# Revit family: 63_UN_Trunk_Maxos Fusion Trunk_Signify
name_source: partatom
category: Lighting Fixtures
units: mm (PartAtom-declared; Revit-internal decimal feet)

## family parameters
Always vertical = Yes
Cut with Voids When Loaded = No
Light Source = No
OmniClass Number = 23.80.70.11.14.11
OmniClass Title = Downlights
Part Type = Normal
Room Calculation Point = Yes
Round Connector Dimension = Use Diameter
Shared = No
Work Plane-Based = No

## types (3) — shared parameters
Apparent Load = 0 VA
Assembly Code = 63.0
ETIM Code = ETIMCODE
GTIN Code = GTINCODE
H1 = 41 mm  [stored 0.134514 ft]
Housing_Material = Laminate, White
IK Value = IK02
IP Value = IP20
ISBN Code = ISBNCODE
IfcExportAs = IfcLightFixtureType
IfcExportType = USERDEFINED
L2 = 62 mm  [stored 0.203412 ft]
Lamp = LED
Manufacturer = Signify
Model = Maxos Fusion Trunk
URL = https://www.ivlibrary.com
Voltage = 0 V
Wattage Comments = 0

## per-type parameters (varying)
| type | L1 |
| L1138 | 1138 mm  [stored 3.7336 ft] |
| L2276 | 2276 mm  [stored 7.46719 ft] |
| L4452 | 4452 mm  [stored 14.6063 ft] |

note: column(s) folded — value = type name in every type: Type Comments

note: [stored X ft] marks values corroborated as IEEE doubles in the binary element streams (Revit-internal decimal feet)

## geometry (parser evidence)
native form markers: Sweep x8
no freeform markers — native parametric forms only
